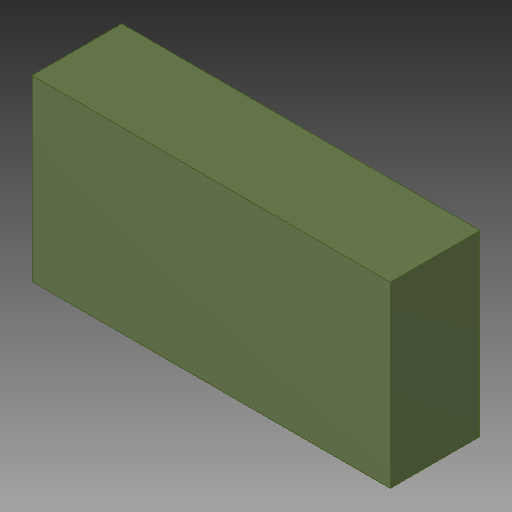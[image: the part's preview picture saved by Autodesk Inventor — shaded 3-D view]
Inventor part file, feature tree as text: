
AUTODESK INVENTOR PART (.ipt)
format: ipt  version: 2019 (Build 230136000, 136)  size: 88,064 bytes
history: native  units: in
note: dims shown in document units (in); Inventor stores cm internally (conversion verified against a paired STEP export)
features: extrude x1, other x1
ambient origin geometry x8: Origin, YZ Plane, XZ Plane, XY Plane, X Axis, Y Axis, Z Axis, Center Point
bodies: Solid1 (feature_tree)
feature tree (2):
  extrude  "Extrusion1"  Depth=0.0394in TaperAngle=0.0deg
  other  "M0805, 200_12"
